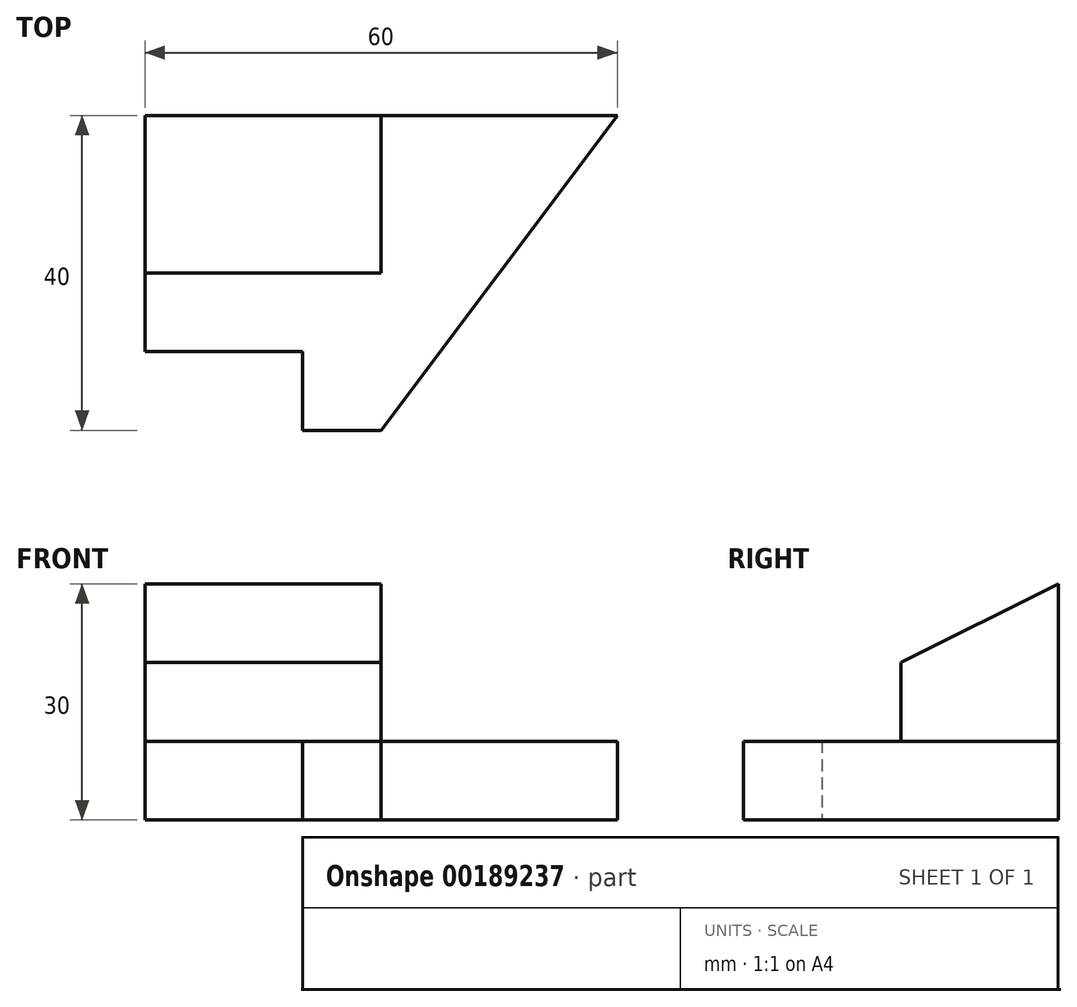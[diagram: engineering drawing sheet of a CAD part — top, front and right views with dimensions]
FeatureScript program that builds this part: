
annotation { "Feature Type Name" : "Feature", "Feature Type Description" : "" }
export const myFeature = defineFeature(function(context is Context, id is Id, definition is map)
    precondition{}
    {
        {
            var Q0;
            Q0=qCreatedBy(makeId("Top.planeOp"),FACE);
            var sketch = newSketch(context, id + "F0", { "sketchPlane" : qUnion([Q0])});
            skLineSegment(sketch, "E0", {"start": v(0, 0) * mm, "end": v(0, 30) * mm});
            skLineSegment(sketch, "E1", {"start": v(0, 30) * mm, "end": v(60, 30) * mm});
            skLineSegment(sketch, "E2", {"start": v(60, 30) * mm, "end": v(30, -10) * mm});
            skLineSegment(sketch, "E3", {"start": v(30, -10) * mm, "end": v(20, -10) * mm});
            skLineSegment(sketch, "E4", {"start": v(20, -10) * mm, "end": v(20, 0) * mm});
            skLineSegment(sketch, "E5", {"start": v(20, 0) * mm, "end": v(0, 0) * mm});
            skSolve(sketch);
        }
        {
            var Q0;
            Q0=makeQuery(id+"F0.imprint","IMPRINT",FACE,{"disambiguationData":[TD([[makeQuery(id+"F0.imprint","IMPRINT",EDGE,{"derivedFrom":sQuery(id+"F0.wireOp",EDGE,"E0")}),-1.0]])]});
            extrude(context, id + "F1", {"entities" : qUnion([Q0]), "depth" : 10 * mm});
        }
        {
            var Q0;
            Q0=makeQuery(id+"F1.opExtrude","CAP_FACE",FACE,{"disambiguationData":[OSD([sQuery(id+"F0.wireOp",EDGE,"E0"),sQuery(id+"F0.wireOp",EDGE,"E1"),sQuery(id+"F0.wireOp",EDGE,"E2"),sQuery(id+"F0.wireOp",EDGE,"E3"),sQuery(id+"F0.wireOp",EDGE,"E4"),sQuery(id+"F0.wireOp",EDGE,"E5")])],"isStart":false});
            var sketch = newSketch(context, id + "F2", { "sketchPlane" : qUnion([Q0])});
            skLineSegment(sketch, "E6.bottom", {"start": v(0, 30) * mm, "end": v(30, 30) * mm});
            skLineSegment(sketch, "E6.top", {"start": v(0, 10) * mm, "end": v(30, 10) * mm});
            skLineSegment(sketch, "E6.left", {"start": v(0, 30) * mm, "end": v(0, 10) * mm});
            skLineSegment(sketch, "E6.right", {"start": v(30, 30) * mm, "end": v(30, 10) * mm});
            skSolve(sketch);
        }
        {
            var Q0;
            Q0=makeQuery(id+"F2.imprint","IMPRINT",FACE,{"disambiguationData":[TD([[makeQuery(id+"F2.imprint","IMPRINT",EDGE,{"derivedFrom":sQuery(id+"F2.wireOp",EDGE,"E6.bottom")}),-1.0]])]});
            extrude(context, id + "F3", {"entities" : qUnion([Q0]), "operationType" : NewBodyOperationType.ADD, "depth" : 20 * mm});
        }
        {
            var Q0;
            Q0=makeQuery(id+"F3.opExtrude","CAP_EDGE",EDGE,{"disambiguationData":[OSD([sQuery(id+"F2.wireOp",EDGE,"E6.top")])],"isStart":false});
            chamfer(context, id + "F4", {"entities" : qUnion([Q0]), "chamferType" : ChamferType.TWO_OFFSETS, "width1" : 20 * mm, "oppositeDirection" : false, "width2" : 10 * mm, "tangentPropagation" : true});
        }
    });
